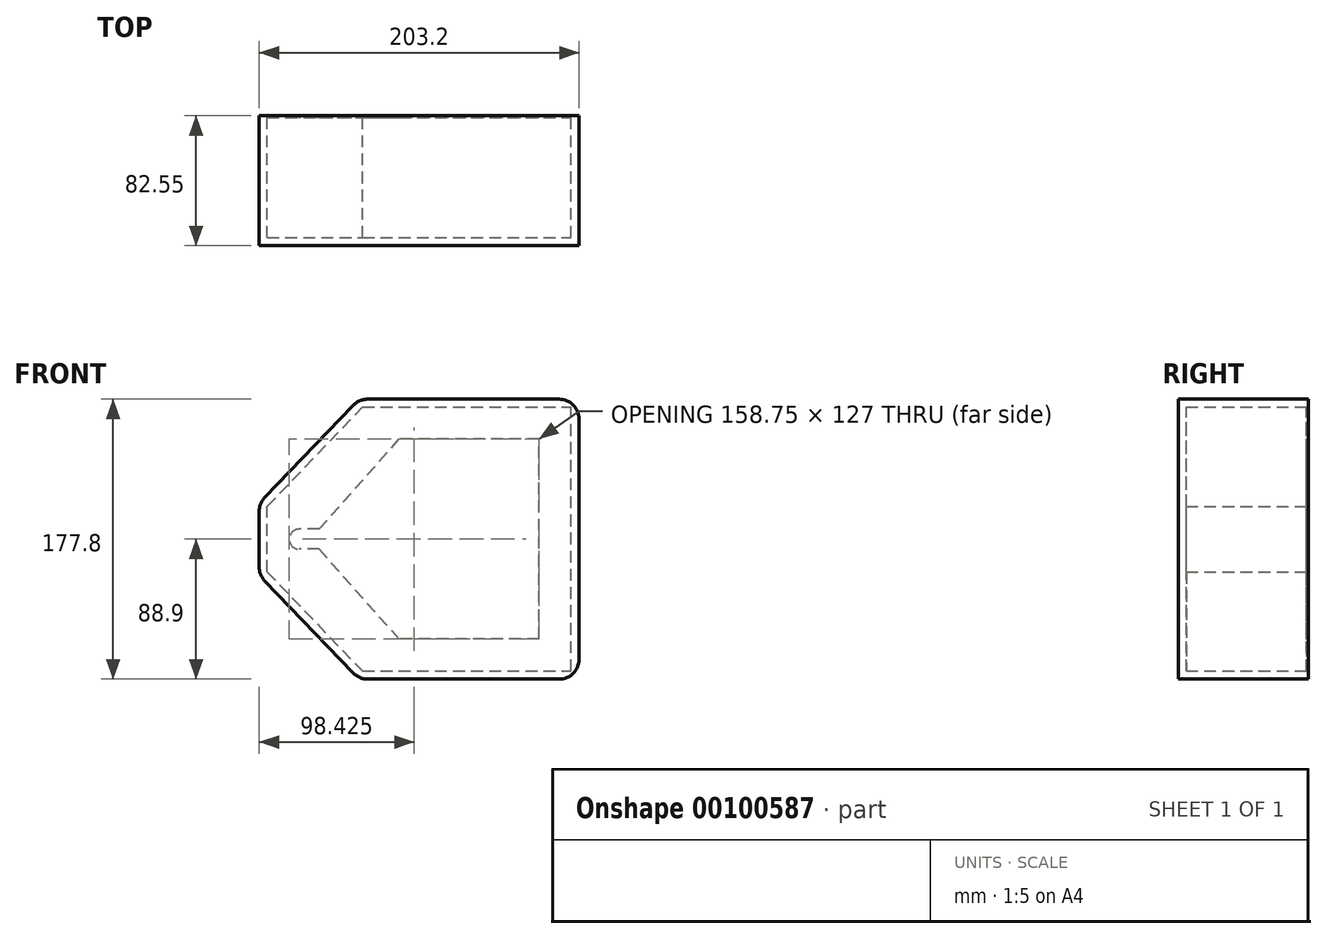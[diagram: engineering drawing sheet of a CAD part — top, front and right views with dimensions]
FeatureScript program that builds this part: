
annotation { "Feature Type Name" : "Feature", "Feature Type Description" : "" }
export const myFeature = defineFeature(function(context is Context, id is Id, definition is map)
    precondition{}
    {
        {
            var Q0;
            Q0=qCreatedBy(makeId("Front.planeOp"),FACE);
            var sketch = newSketch(context, id + "F0", { "sketchPlane" : qUnion([Q0])});
            skLineSegment(sketch, "E0", {"start": v(12.7, 6.35) * mm, "end": v(63.5, 63.5) * mm});
            skArc(sketch, "E1", {"start": v(0, 6.35) * mm, "mid": v(-6.35, 0) * mm, "end": v(0, -6.35) * mm});
            skLineSegment(sketch, "E2", {"start": v(12.7, 6.35) * mm, "end": v(0, 6.35) * mm});
            skLineSegment(sketch, "E3", {"start": v(0, 6.35) * mm, "end": v(0, -6.35) * mm, "construction": true});
            skPoint(sketch, "E4.centerSnap0", {"position": v(-6.35, 0) * mm});
            skLineSegment(sketch, "E5", {"start": v(-25.4, 0) * mm, "end": v(-25.4, 22.88) * mm});
            skLineSegment(sketch, "E6", {"start": v(-25.4, 22.88) * mm, "end": v(38.1, 88.9) * mm});
            skLineSegment(sketch, "E7", {"start": v(38.1, 88.9) * mm, "end": v(177.8, 88.9) * mm});
            skLineSegment(sketch, "E8", {"start": v(177.8, 88.9) * mm, "end": v(177.8, 0) * mm});
            skLineSegment(sketch, "E9", {"start": v(152.4, 0) * mm, "end": v(152.4, 63.5) * mm});
            skLineSegment(sketch, "E10", {"start": v(152.4, 63.5) * mm, "end": v(63.5, 63.5) * mm});
            skArc(sketch, "E11.MirrorCS", {"start": v(0, -6.35) * mm, "mid": v(-6.35, 0) * mm, "end": v(0, 6.35) * mm});
            skLineSegment(sketch, "E12.MirrorCS", {"start": v(0, -6.35) * mm, "end": v(0, 6.35) * mm, "construction": true});
            skLineSegment(sketch, "E13.MirrorCS", {"start": v(152.4, -63.5) * mm, "end": v(63.5, -63.5) * mm});
            skLineSegment(sketch, "E14.MirrorCS", {"start": v(12.7, -6.35) * mm, "end": v(0, -6.35) * mm});
            skLineSegment(sketch, "E15.MirrorCS", {"start": v(-25.4, 0) * mm, "end": v(-25.4, -22.88) * mm});
            skLineSegment(sketch, "E16.MirrorCS", {"start": v(38.1, -88.9) * mm, "end": v(177.8, -88.9) * mm});
            skLineSegment(sketch, "E17.MirrorCS", {"start": v(152.4, 0) * mm, "end": v(152.4, -63.5) * mm});
            skLineSegment(sketch, "E18.MirrorCS", {"start": v(-25.4, -22.88) * mm, "end": v(38.1, -88.9) * mm});
            skLineSegment(sketch, "E19.MirrorCS", {"start": v(177.8, -88.9) * mm, "end": v(177.8, 0) * mm});
            skLineSegment(sketch, "E20.MirrorCS", {"start": v(12.7, -6.35) * mm, "end": v(63.5, -63.5) * mm});
            skSolve(sketch);
        }
        {
            var Q0;
            Q0=makeQuery(id+"F0.imprint","IMPRINT",FACE,{"disambiguationData":[TD([[makeQuery(id+"F0.imprint","IMPRINT",EDGE,{"derivedFrom":sQuery(id+"F0.wireOp",EDGE,"E0")}),1.0]])]});
            extrude(context, id + "F1", {"entities" : qUnion([Q0]), "depth" : 1.27 * mm});
        }
        {
            var Q0;
            Q0=makeQuery(id+"F1.opExtrude","CAP_FACE",FACE,{"disambiguationData":[OSD([sQuery(id+"F0.wireOp",EDGE,"E0"),sQuery(id+"F0.wireOp",EDGE,"E2"),sQuery(id+"F0.wireOp",EDGE,"E5"),sQuery(id+"F0.wireOp",EDGE,"E6"),sQuery(id+"F0.wireOp",EDGE,"E7"),sQuery(id+"F0.wireOp",EDGE,"E8"),sQuery(id+"F0.wireOp",EDGE,"E9"),sQuery(id+"F0.wireOp",EDGE,"E10"),sQuery(id+"F0.wireOp",EDGE,"E11.MirrorCS"),sQuery(id+"F0.wireOp",EDGE,"E13.MirrorCS"),sQuery(id+"F0.wireOp",EDGE,"E14.MirrorCS"),sQuery(id+"F0.wireOp",EDGE,"E15.MirrorCS"),sQuery(id+"F0.wireOp",EDGE,"E16.MirrorCS"),sQuery(id+"F0.wireOp",EDGE,"E17.MirrorCS"),sQuery(id+"F0.wireOp",EDGE,"E18.MirrorCS"),sQuery(id+"F0.wireOp",EDGE,"E19.MirrorCS"),sQuery(id+"F0.wireOp",EDGE,"E20.MirrorCS")])],"isStart":false});
            var sketch = newSketch(context, id + "F2", { "sketchPlane" : qUnion([Q0])});
            skLineSegment(sketch, "E21.0", {"start": v(-20.32, -20.84) * mm, "end": v(-20.32, 20.84) * mm});
            skLineSegment(sketch, "E21.1", {"start": v(40.26, 83.82) * mm, "end": v(172.72, 83.82) * mm});
            skLineSegment(sketch, "E21.2", {"start": v(172.72, -83.82) * mm, "end": v(172.72, 83.82) * mm});
            skLineSegment(sketch, "E21.3", {"start": v(-20.32, 20.84) * mm, "end": v(40.26, 83.82) * mm});
            skLineSegment(sketch, "E21.4", {"start": v(40.26, -83.82) * mm, "end": v(172.72, -83.82) * mm});
            skLineSegment(sketch, "E21.5", {"start": v(-20.32, -20.84) * mm, "end": v(40.26, -83.82) * mm});
            skSolve(sketch);
        }
        {
            var Q0;
            Q0=makeQuery(id+"F2.imprint","IMPRINT",FACE,{"disambiguationData":[TD([[makeQuery(id+"F2.imprint","IMPRINT",EDGE,{"derivedFrom":sQuery(id+"F2.wireOp",EDGE,"E21.0")}),1.0]])]});
            extrude(context, id + "F3", {"entities" : qUnion([Q0]), "operationType" : NewBodyOperationType.ADD, "depth" : 76.2 * mm});
        }
        {
            var Q0;
            Q0=makeQuery(id+"F3.opExtrude","CAP_FACE",FACE,{"disambiguationData":[OSD([sQuery(id+"F0.wireOp",EDGE,"E5"),sQuery(id+"F0.wireOp",EDGE,"E6"),sQuery(id+"F0.wireOp",EDGE,"E7"),sQuery(id+"F0.wireOp",EDGE,"E8"),sQuery(id+"F0.wireOp",EDGE,"E15.MirrorCS"),sQuery(id+"F0.wireOp",EDGE,"E16.MirrorCS"),sQuery(id+"F0.wireOp",EDGE,"E18.MirrorCS"),sQuery(id+"F0.wireOp",EDGE,"E19.MirrorCS"),sQuery(id+"F2.wireOp",EDGE,"E21.0"),sQuery(id+"F2.wireOp",EDGE,"E21.1"),sQuery(id+"F2.wireOp",EDGE,"E21.2"),sQuery(id+"F2.wireOp",EDGE,"E21.3"),sQuery(id+"F2.wireOp",EDGE,"E21.4"),sQuery(id+"F2.wireOp",EDGE,"E21.5")])],"isStart":false});
            var sketch = newSketch(context, id + "F4", { "sketchPlane" : qUnion([Q0])});
            skSolve(sketch);
        }
        {
            var Q0;
            Q0 = qSketchRegion(id + "F4", true);
            var Q1;
            Q1=makeQuery(id+"F4.imprint","IMPRINT",FACE,{"disambiguationData":[TD([[makeQuery(id+"F4.imprint","IMPRINT",EDGE,{"derivedFrom":makeQuery(id+"F3.opExtrude","CAP_EDGE",EDGE,{"disambiguationData":[OSD([sQuery(id+"F2.wireOp",EDGE,"E21.0")])],"isStart":false})}),-1.0]])]});
            var Q2;
            Q2=makeQuery(id+"F4.imprint","IMPRINT",FACE,{"disambiguationData":[TD([[makeQuery(id+"F4.imprint","IMPRINT",EDGE,{"derivedFrom":makeQuery(id+"F3.opExtrude","CAP_EDGE",EDGE,{"disambiguationData":[OSD([sQuery(id+"F2.wireOp",EDGE,"E21.0")])],"isStart":false})}),1.0]])]});
            extrude(context, id + "F5", {"entities" : qUnion([Q0, Q1, Q2]), "operationType" : NewBodyOperationType.ADD, "depth" : 5.08 * mm});
        }
        {
            var Q0;
            {var subQ0=sQuery(id+"F0.wireOp",EDGE,"E15.MirrorCS");var subQ1=sQuery(id+"F0.wireOp",EDGE,"E6");var subQ2=sQuery(id+"F0.wireOp",EDGE,"E5");Q0=makeQuery(id+"F5.boolean.opBoolean","MERGE",EDGE,{"derivedFrom":[makeQuery(id+"F3.boolean.opBoolean","MERGE",EDGE,{"derivedFrom":[makeQuery(id+"F1.opExtrude","SWEPT_EDGE",EDGE,{"disambiguationData":[OSD([subQ2,subQ1])]}),makeQuery(id+"F3.opExtrude","SWEPT_EDGE",EDGE,{"disambiguationData":[OSD([subQ2,subQ1,subQ0])]})]}),makeQuery(id+"F5.opExtrude","SWEPT_EDGE",EDGE,{"disambiguationData":[OSD([subQ2,subQ1,subQ0])]})]});}
            var Q1;
            {var subQ0=sQuery(id+"F0.wireOp",EDGE,"E18.MirrorCS");var subQ1=sQuery(id+"F0.wireOp",EDGE,"E15.MirrorCS");var subQ2=sQuery(id+"F0.wireOp",EDGE,"E5");Q1=makeQuery(id+"F5.boolean.opBoolean","MERGE",EDGE,{"derivedFrom":[makeQuery(id+"F3.boolean.opBoolean","MERGE",EDGE,{"derivedFrom":[makeQuery(id+"F1.opExtrude","SWEPT_EDGE",EDGE,{"disambiguationData":[OSD([subQ1,subQ0])]}),makeQuery(id+"F3.opExtrude","SWEPT_EDGE",EDGE,{"disambiguationData":[OSD([subQ2,subQ1,subQ0])]})]}),makeQuery(id+"F5.opExtrude","SWEPT_EDGE",EDGE,{"disambiguationData":[OSD([subQ2,subQ1,subQ0])]})]});}
            var Q2;
            {var subQ0=sQuery(id+"F0.wireOp",EDGE,"E7");var subQ1=sQuery(id+"F0.wireOp",EDGE,"E6");Q2=makeQuery(id+"F5.boolean.opBoolean","MERGE",EDGE,{"derivedFrom":[makeQuery(id+"F3.boolean.opBoolean","MERGE",EDGE,{"derivedFrom":[makeQuery(id+"F1.opExtrude","SWEPT_EDGE",EDGE,{"disambiguationData":[OSD([subQ1,subQ0])]}),makeQuery(id+"F3.opExtrude","SWEPT_EDGE",EDGE,{"disambiguationData":[OSD([subQ1,subQ0])]})]}),makeQuery(id+"F5.opExtrude","SWEPT_EDGE",EDGE,{"disambiguationData":[OSD([subQ1,subQ0])]})]});}
            var Q3;
            {var subQ0=sQuery(id+"F0.wireOp",EDGE,"E18.MirrorCS");var subQ1=sQuery(id+"F0.wireOp",EDGE,"E16.MirrorCS");Q3=makeQuery(id+"F5.boolean.opBoolean","MERGE",EDGE,{"derivedFrom":[makeQuery(id+"F3.boolean.opBoolean","MERGE",EDGE,{"derivedFrom":[makeQuery(id+"F1.opExtrude","SWEPT_EDGE",EDGE,{"disambiguationData":[OSD([subQ1,subQ0])]}),makeQuery(id+"F3.opExtrude","SWEPT_EDGE",EDGE,{"disambiguationData":[OSD([subQ1,subQ0])]})]}),makeQuery(id+"F5.opExtrude","SWEPT_EDGE",EDGE,{"disambiguationData":[OSD([subQ1,subQ0])]})]});}
            fillet(context, id + "F6", {"entities" : qUnion([Q0, Q1, Q2, Q3]), "radius" : 12.7 * mm, "tangentPropagation" : true, "allowEdgeOverflow" : false});
        }
        {
            var Q0;
            {var subQ0=sQuery(id+"F0.wireOp",EDGE,"E19.MirrorCS");var subQ1=sQuery(id+"F0.wireOp",EDGE,"E8");var subQ2=sQuery(id+"F0.wireOp",EDGE,"E7");Q0=makeQuery(id+"F5.boolean.opBoolean","MERGE",EDGE,{"derivedFrom":[makeQuery(id+"F3.boolean.opBoolean","MERGE",EDGE,{"derivedFrom":[makeQuery(id+"F1.opExtrude","SWEPT_EDGE",EDGE,{"disambiguationData":[OSD([subQ2,subQ1])]}),makeQuery(id+"F3.opExtrude","SWEPT_EDGE",EDGE,{"disambiguationData":[OSD([subQ2,subQ1,subQ0])]})]}),makeQuery(id+"F5.opExtrude","SWEPT_EDGE",EDGE,{"disambiguationData":[OSD([subQ2,subQ1,subQ0])]})]});}
            var Q1;
            {var subQ0=sQuery(id+"F0.wireOp",EDGE,"E19.MirrorCS");var subQ1=sQuery(id+"F0.wireOp",EDGE,"E16.MirrorCS");var subQ2=sQuery(id+"F0.wireOp",EDGE,"E8");Q1=makeQuery(id+"F5.boolean.opBoolean","MERGE",EDGE,{"derivedFrom":[makeQuery(id+"F3.boolean.opBoolean","MERGE",EDGE,{"derivedFrom":[makeQuery(id+"F1.opExtrude","SWEPT_EDGE",EDGE,{"disambiguationData":[OSD([subQ1,subQ0])]}),makeQuery(id+"F3.opExtrude","SWEPT_EDGE",EDGE,{"disambiguationData":[OSD([subQ2,subQ1,subQ0])]})]}),makeQuery(id+"F5.opExtrude","SWEPT_EDGE",EDGE,{"disambiguationData":[OSD([subQ2,subQ1,subQ0])]})]});}
            fillet(context, id + "F7", {"entities" : qUnion([Q0, Q1]), "radius" : 12.7 * mm, "tangentPropagation" : true, "allowEdgeOverflow" : false});
        }
    });
